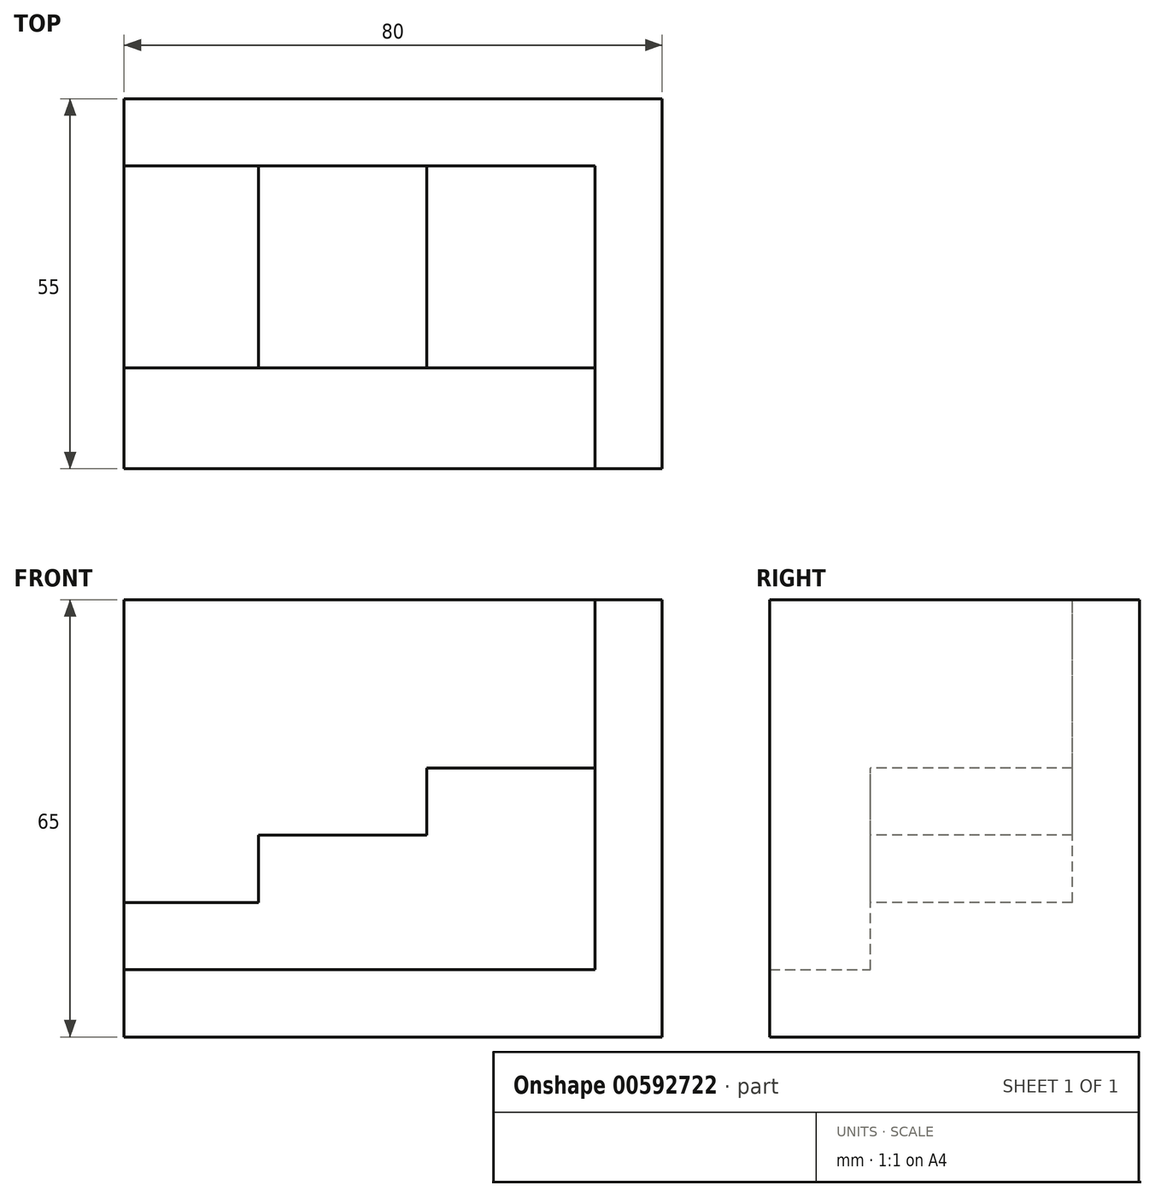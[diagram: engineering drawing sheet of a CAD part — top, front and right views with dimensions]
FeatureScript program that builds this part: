
annotation { "Feature Type Name" : "Feature", "Feature Type Description" : "" }
export const myFeature = defineFeature(function(context is Context, id is Id, definition is map)
    precondition{}
    {
        {
            var Q0;
            Q0=qCreatedBy(makeId("Front.planeOp"),FACE);
            var sketch = newSketch(context, id + "F0", { "sketchPlane" : qUnion([Q0])});
            skLineSegment(sketch, "E0.bottom", {"start": v(-40, 32.5) * mm, "end": v(40, 32.5) * mm});
            skLineSegment(sketch, "E0.top", {"start": v(-40, -32.5) * mm, "end": v(40, -32.5) * mm});
            skLineSegment(sketch, "E0.left", {"start": v(-40, 32.5) * mm, "end": v(-40, -32.5) * mm});
            skLineSegment(sketch, "E0.right", {"start": v(40, 32.5) * mm, "end": v(40, -32.5) * mm});
            skPoint(sketch, "E0.middle", {"position": v(0, 0) * mm});
            skSolve(sketch);
        }
        {
            var Q0;
            Q0 = qSketchRegion(id + "F0", true);
            extrude(context, id + "F1", {"entities" : qUnion([Q0]), "depth" : 55 * mm, "offsetDistance" : 25 * mm});
        }
        {
            var Q0;
            Q0=makeQuery(id+"F1.opExtrude","SWEPT_FACE",FACE,{"disambiguationData":[OSD([sQuery(id+"F0.wireOp",EDGE,"E0.bottom")])]});
            var sketch = newSketch(context, id + "F2", { "sketchPlane" : qUnion([Q0])});
            skLineSegment(sketch, "E1", {"start": v(-40, -10) * mm, "end": v(30, -10) * mm});
            skLineSegment(sketch, "E2", {"start": v(30, -10) * mm, "end": v(30, -55) * mm});
            skLineSegment(sketch, "E3", {"start": v(-40, -10) * mm, "end": v(-40, 0) * mm});
            skLineSegment(sketch, "E4", {"start": v(-40, 0) * mm, "end": v(40, 0) * mm});
            skLineSegment(sketch, "E5", {"start": v(40, 0) * mm, "end": v(40, -55) * mm});
            skLineSegment(sketch, "E6", {"start": v(40, -55) * mm, "end": v(30, -55) * mm});
            skSolve(sketch);
        }
        {
            var Q0;
            {var subQ0=sQuery(id+"F2.wireOp",EDGE,"E1");Q0=makeQuery(id+"F2.imprint","IMPRINT",FACE,{"disambiguationData":[TD([[makeQuery(id+"F2.imprint","IMPRINT",EDGE,{"derivedFrom":subQ0}),-1.0]])]});}
            extrude(context, id + "F3", {"entities" : qUnion([Q0]), "operationType" : NewBodyOperationType.REMOVE, "oppositeDirection" : true, "depth" : 10 * mm, "offsetDistance" : 25 * mm});
        }
        {
            var Q0;
            Q0=makeQuery(id+"F3.boolean.opBoolean","COPY",FACE,{"derivedFrom":makeQuery(id+"F3.opExtrude","CAP_FACE",FACE,{"disambiguationData":[OSD([sQuery(id+"F0.wireOp",EDGE,"E0.bottom"),sQuery(id+"F0.wireOp",EDGE,"E0.left"),sQuery(id+"F2.wireOp",EDGE,"E1"),sQuery(id+"F2.wireOp",EDGE,"E2")])],"isStart":false})});
            var sketch = newSketch(context, id + "F4", { "sketchPlane" : qUnion([Q0])});
            skLineSegment(sketch, "E7", {"start": v(30, -40) * mm, "end": v(-40, -40) * mm});
            skLineSegment(sketch, "E8", {"start": v(30, -40) * mm, "end": v(30, -55) * mm});
            skLineSegment(sketch, "E9", {"start": v(30, -55) * mm, "end": v(-40, -55) * mm});
            skLineSegment(sketch, "E10", {"start": v(-40, -55) * mm, "end": v(-40, -40) * mm});
            skSolve(sketch);
        }
        {
            var Q0;
            Q0 = qSketchRegion(id + "F4", true);
            extrude(context, id + "F5", {"entities" : qUnion([Q0]), "operationType" : NewBodyOperationType.REMOVE, "oppositeDirection" : true, "depth" : 45 * mm, "offsetDistance" : 25 * mm});
        }
        {
            var Q0;
            Q0=makeQuery(id+"F5.boolean.opBoolean","COPY",FACE,{"derivedFrom":makeQuery(id+"F5.opExtrude","SWEPT_FACE",FACE,{"disambiguationData":[OSD([sQuery(id+"F4.wireOp",EDGE,"E7")])]})});
            var sketch = newSketch(context, id + "F6", { "sketchPlane" : qUnion([Q0])});
            skLineSegment(sketch, "E11", {"start": v(-40, -12.5) * mm, "end": v(-20, -12.5) * mm});
            skLineSegment(sketch, "E12", {"start": v(-20, -12.5) * mm, "end": v(-20, -2.5) * mm});
            skLineSegment(sketch, "E13", {"start": v(-20, -2.5) * mm, "end": v(5, -2.5) * mm});
            skLineSegment(sketch, "E14", {"start": v(5, -2.5) * mm, "end": v(5, 7.5) * mm});
            skLineSegment(sketch, "E15", {"start": v(5, 7.5) * mm, "end": v(30, 7.5) * mm});
            skLineSegment(sketch, "E16", {"start": v(-40, -12.5) * mm, "end": v(-40, -22.5) * mm});
            skLineSegment(sketch, "E17", {"start": v(-40, -22.5) * mm, "end": v(30, -22.5) * mm});
            skLineSegment(sketch, "E18", {"start": v(30, -22.5) * mm, "end": v(30, 7.5) * mm});
            skSolve(sketch);
        }
        {
            var Q0;
            {var subQ0=sQuery(id+"F6.wireOp",EDGE,"E11");Q0=makeQuery(id+"F6.imprint","IMPRINT",FACE,{"disambiguationData":[TD([[makeQuery(id+"F6.imprint","IMPRINT",EDGE,{"derivedFrom":subQ0}),1.0]])]});}
            extrude(context, id + "F7", {"entities" : qUnion([Q0]), "operationType" : NewBodyOperationType.REMOVE, "oppositeDirection" : true, "depth" : 30 * mm, "offsetDistance" : 25 * mm});
        }
    });
